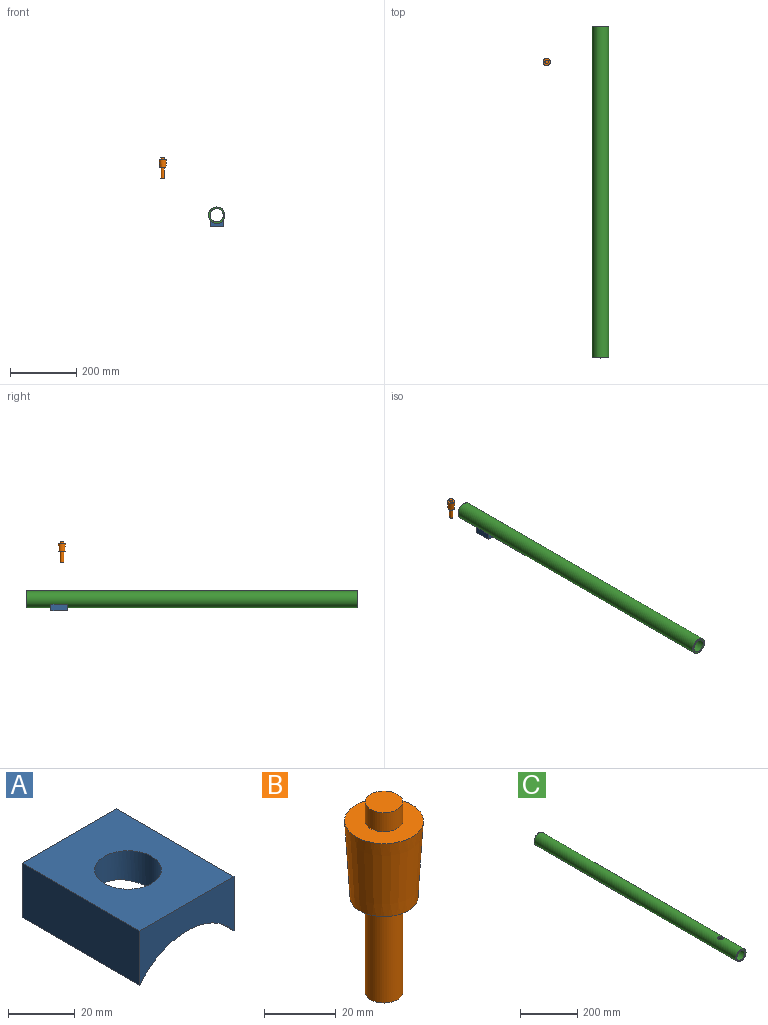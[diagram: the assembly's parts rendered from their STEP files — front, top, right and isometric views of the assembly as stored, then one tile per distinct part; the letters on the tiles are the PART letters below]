
ASSEMBLY  parts=3 mates=1
PART A: 7 faces, bbox 40x50x19.9 mm
  f0: cylinder r=25mm len=50mm, axis (0,1,0), area 1997.1mm2, adj f1,f2,f3,f5,f6
  f1: plane 50x19.91mm, normal (-1,0,0), area 995.6mm2, adj f0,f3,f4,f5
  f2: plane 50x19.91mm, normal (1,0,0), area 995.6mm2, adj f0,f3,f4,f5
  f3: plane 40x19.91mm, normal (0,1,0), area 516.9mm2, adj f0,f1,f2,f4
  f4: plane 50x40mm, normal (0,0,1), area 1685.8mm2, adj f1,f2,f3,f5,f6
  f5: plane 40x19.91mm, normal (0,-1,0), area 516.9mm2, adj f0,f1,f2,f4
  f6: cylinder r=10mm len=20mm, axis (0,0,-1), area 687.5mm2, adj f0,f4
PART B: 7 faces, bbox 22x22x65 mm
  f0: plane 22x22mm, normal (0,0,1), area 293.5mm2, adj f2,f5
  f1: plane 19x19mm, normal (0,0,-1), area 196.9mm2, adj f2,f4
  f2: cone r=11mm half-angle=3.3deg, axis (0,0,1), area 1677.3mm2, adj f0,f1
  f3: plane 10.5x10.5mm, normal (0,0,-1), area 86.6mm2, adj f4
  f4: cylinder r=5.25mm len=32.5mm, axis (0,0,-1), area 1072.1mm2, adj f1,f3
  f5: cylinder r=5.25mm len=10.5mm, axis (0,0,-1), area 214.4mm2, adj f0,f6
  f6: plane 10.5x10.5mm, normal (0,0,1), area 86.6mm2, adj f5
PART C: 5 faces, bbox 50x1000x50 mm
  f0: cylinder r=25mm len=1000mm, axis (0,-1,0), area 156758.8mm2, adj f2,f3,f4
  f1: cylinder r=20mm len=1000mm, axis (0,-1,0), area 125337.9mm2, adj f2,f3,f4
  f2: plane 50x50mm, normal (0,1,0), area 706.9mm2, adj f0,f1
  f3: plane 50x50mm, normal (0,-1,0), area 706.9mm2, adj f0,f1
  f4: cylinder r=10mm len=20mm, axis (0,0,-1), area 331.9mm2, adj f0,f1
PLACE A rot(axis=(1,0,0),180deg) t=(-56.96,478.19,-8.64)mm
PLACE B t=(-219.51,494.83,149.09)mm
PLACE C rot(axis=(1,0,0),180deg) t=(-56.96,603.2,6.36)mm
MATE slider C.f0 <-> A.f0  axis (0,1,0) through (-56.96,103.2,6.36)mm
